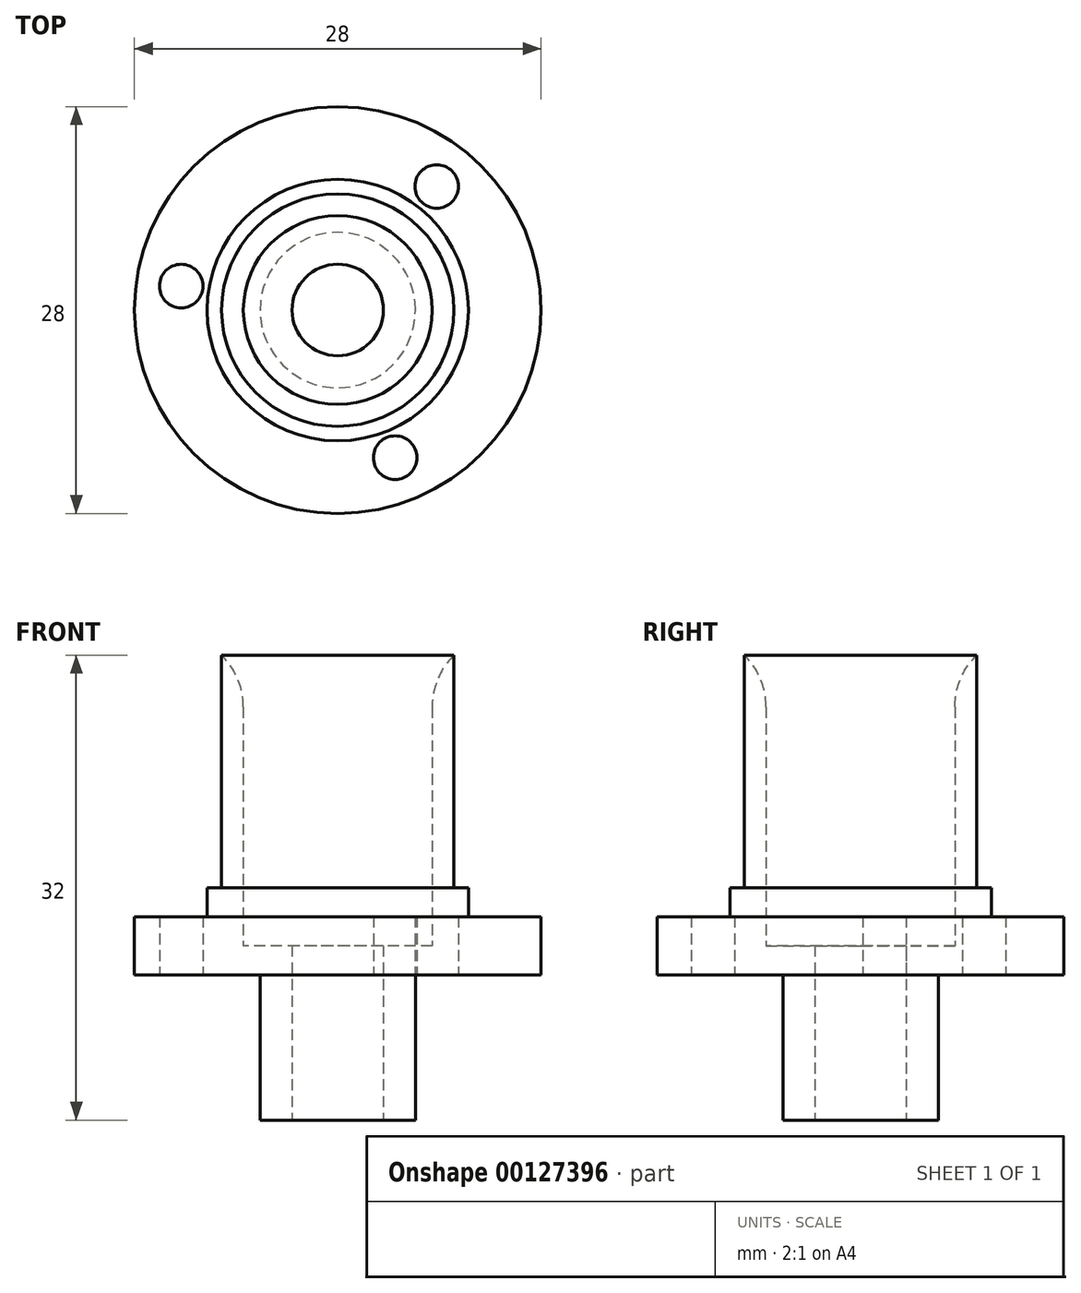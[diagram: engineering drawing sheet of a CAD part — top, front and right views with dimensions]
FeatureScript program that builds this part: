
annotation { "Feature Type Name" : "Feature", "Feature Type Description" : "" }
export const myFeature = defineFeature(function(context is Context, id is Id, definition is map)
    precondition{}
    {
        {
            var Q0;
            Q0=qCreatedBy(makeId("Top.planeOp"),FACE);
            var sketch = newSketch(context, id + "F0", { "sketchPlane" : qUnion([Q0])});
            skCircle(sketch, "E0", {"center": v(0, 0) * mm, "radius": 14 * mm});
            skCircle(sketch, "E1", {"center": v(0, 0) * mm, "radius": 3.15 * mm});
            skSolve(sketch);
        }
        {
            var Q0;
            Q0=makeQuery(id+"F0.imprint","IMPRINT",FACE,{"disambiguationData":[TD([[makeQuery(id+"F0.imprint","IMPRINT",EDGE,{"derivedFrom":sQuery(id+"F0.wireOp",EDGE,"E0")}),1.0]])]});
            extrude(context, id + "F1", {"entities" : qUnion([Q0]), "depth" : 4 * mm});
        }
        {
            var Q0;
            Q0=qCreatedBy(makeId("Top.planeOp"),FACE);
            var sketch = newSketch(context, id + "F2", { "sketchPlane" : qUnion([Q0])});
            skCircle(sketch, "E2", {"center": v(0, 0) * mm, "radius": 9 * mm});
            skSolve(sketch);
        }
        {
            var Q0;
            Q0=makeQuery(id+"F2.imprint","IMPRINT",FACE,{"disambiguationData":[TD([[makeQuery(id+"F2.imprint","IMPRINT",EDGE,{"derivedFrom":sQuery(id+"F2.wireOp",EDGE,"E2")}),1.0]])]});
            extrude(context, id + "F3", {"entities" : qUnion([Q0]), "operationType" : NewBodyOperationType.ADD, "depth" : 6 * mm});
        }
        {
            var Q0;
            Q0=qCreatedBy(makeId("Top.planeOp"),FACE);
            var sketch = newSketch(context, id + "F4", { "sketchPlane" : qUnion([Q0])});
            skCircle(sketch, "E3", {"center": v(0, 0) * mm, "radius": 8 * mm});
            skSolve(sketch);
        }
        {
            var Q0;
            Q0=makeQuery(id+"F4.imprint","IMPRINT",FACE,{"disambiguationData":[TD([[makeQuery(id+"F4.imprint","IMPRINT",EDGE,{"derivedFrom":sQuery(id+"F4.wireOp",EDGE,"E3")}),1.0]])]});
            extrude(context, id + "F5", {"entities" : qUnion([Q0]), "operationType" : NewBodyOperationType.ADD, "depth" : 22 * mm});
        }
        {
            var Q0;
            Q0=qCreatedBy(makeId("Top.planeOp"),FACE);
            var sketch = newSketch(context, id + "F6", { "sketchPlane" : qUnion([Q0])});
            skCircle(sketch, "E4", {"center": v(0, 0) * mm, "radius": 6.5 * mm});
            skSolve(sketch);
        }
        {
            var Q0;
            Q0=makeQuery(id+"F6.imprint","IMPRINT",FACE,{"disambiguationData":[TD([[makeQuery(id+"F6.imprint","IMPRINT",EDGE,{"derivedFrom":sQuery(id+"F6.wireOp",EDGE,"E4")}),1.0]])]});
            extrude(context, id + "F7", {"entities" : qUnion([Q0]), "operationType" : NewBodyOperationType.REMOVE, "depth" : 25 * mm});
        }
        {
            var Q0;
            Q0=qCreatedBy(makeId("Top.planeOp"),FACE);
            var sketch = newSketch(context, id + "F8", { "sketchPlane" : qUnion([Q0])});
            skCircle(sketch, "E5.cCircle", {"center": v(0, 0) * mm, "radius": 10.9 * mm, "construction": true});
            skLineSegment(sketch, "E5.0", {"start": v(-10.77, 1.65) * mm, "end": v(6.82, 8.5) * mm});
            skLineSegment(sketch, "E5.1", {"start": v(6.82, 8.5) * mm, "end": v(3.96, -10.16) * mm});
            skLineSegment(sketch, "E5.2", {"start": v(3.96, -10.16) * mm, "end": v(-10.77, 1.65) * mm});
            skCircle(sketch, "E6", {"center": v(3.96, -10.16) * mm, "radius": 1.5 * mm});
            skCircle(sketch, "E7", {"center": v(6.82, 8.5) * mm, "radius": 1.5 * mm});
            skCircle(sketch, "E8", {"center": v(-10.77, 1.65) * mm, "radius": 1.5 * mm});
            skSolve(sketch);
        }
        {
            var Q0;
            Q0=qCreatedBy(makeId("Top.planeOp"),FACE);
            var sketch = newSketch(context, id + "F9", { "sketchPlane" : qUnion([Q0])});
            skCircle(sketch, "E9", {"center": v(0, 0) * mm, "radius": 3.15 * mm});
            skCircle(sketch, "E10", {"center": v(0, 0) * mm, "radius": 5.35 * mm});
            skSolve(sketch);
        }
        {
            var Q0;
            Q0=makeQuery(id+"F0.imprint","IMPRINT",FACE,{"disambiguationData":[TD([[makeQuery(id+"F0.imprint","IMPRINT",EDGE,{"derivedFrom":sQuery(id+"F0.wireOp",EDGE,"E0")}),1.0]])]});
            extrude(context, id + "F10", {"entities" : qUnion([Q0]), "operationType" : NewBodyOperationType.ADD, "depth" : 2 * mm});
        }
        {
            var Q0;
            {var subQ0=sQuery(id+"F8.wireOp",EDGE,"E5.2");var subQ1=sQuery(id+"F8.wireOp",EDGE,"E5.1");var subQ2=makeQuery(id+"F8.imprint","INTERSECT",VERTEX,{"derivedFrom":[subQ1,subQ0]});Q0=makeQuery(id+"F8.imprint","IMPRINT",FACE,{"disambiguationData":[TD([[makeQuery(id+"F8.imprint","IMPRINT",EDGE,{"disambiguationData":[TD([[subQ2,1.0]])],"derivedFrom":subQ1}),1.0]])]});}
            var Q1;
            {var subQ0=sQuery(id+"F8.wireOp",EDGE,"E5.2");var subQ1=sQuery(id+"F8.wireOp",EDGE,"E5.1");var subQ2=makeQuery(id+"F8.imprint","INTERSECT",VERTEX,{"derivedFrom":[subQ1,subQ0]});Q1=makeQuery(id+"F8.imprint","IMPRINT",FACE,{"disambiguationData":[TD([[makeQuery(id+"F8.imprint","IMPRINT",EDGE,{"disambiguationData":[TD([[subQ2,1.0]])],"derivedFrom":subQ1}),-1.0]])]});}
            var Q2;
            {var subQ0=sQuery(id+"F8.wireOp",EDGE,"E5.2");var subQ1=sQuery(id+"F8.wireOp",EDGE,"E5.0");var subQ2=makeQuery(id+"F8.imprint","INTERSECT",VERTEX,{"derivedFrom":[subQ1,subQ0]});Q2=makeQuery(id+"F8.imprint","IMPRINT",FACE,{"disambiguationData":[TD([[makeQuery(id+"F8.imprint","IMPRINT",EDGE,{"disambiguationData":[TD([[subQ2,-1.0]])],"derivedFrom":subQ1}),1.0]])]});}
            var Q3;
            {var subQ0=sQuery(id+"F8.wireOp",EDGE,"E5.2");var subQ1=sQuery(id+"F8.wireOp",EDGE,"E5.0");var subQ2=makeQuery(id+"F8.imprint","INTERSECT",VERTEX,{"derivedFrom":[subQ1,subQ0]});Q3=makeQuery(id+"F8.imprint","IMPRINT",FACE,{"disambiguationData":[TD([[makeQuery(id+"F8.imprint","IMPRINT",EDGE,{"disambiguationData":[TD([[subQ2,-1.0]])],"derivedFrom":subQ1}),-1.0]])]});}
            var Q4;
            {var subQ0=sQuery(id+"F8.wireOp",EDGE,"E5.1");var subQ1=sQuery(id+"F8.wireOp",EDGE,"E5.0");var subQ2=makeQuery(id+"F8.imprint","INTERSECT",VERTEX,{"derivedFrom":[subQ1,subQ0]});Q4=makeQuery(id+"F8.imprint","IMPRINT",FACE,{"disambiguationData":[TD([[makeQuery(id+"F8.imprint","IMPRINT",EDGE,{"disambiguationData":[TD([[subQ2,1.0]])],"derivedFrom":subQ1}),1.0]])]});}
            var Q5;
            {var subQ0=sQuery(id+"F8.wireOp",EDGE,"E5.1");var subQ1=sQuery(id+"F8.wireOp",EDGE,"E5.0");var subQ2=makeQuery(id+"F8.imprint","INTERSECT",VERTEX,{"derivedFrom":[subQ1,subQ0]});Q5=makeQuery(id+"F8.imprint","IMPRINT",FACE,{"disambiguationData":[TD([[makeQuery(id+"F8.imprint","IMPRINT",EDGE,{"disambiguationData":[TD([[subQ2,1.0]])],"derivedFrom":subQ1}),-1.0]])]});}
            extrude(context, id + "F11", {"entities" : qUnion([Q0, Q1, Q2, Q3, Q4, Q5]), "operationType" : NewBodyOperationType.REMOVE, "depth" : 25 * mm});
        }
        {
            var Q0;
            Q0=makeQuery(id+"F9.imprint","IMPRINT",FACE,{"disambiguationData":[TD([[makeQuery(id+"F9.imprint","IMPRINT",EDGE,{"derivedFrom":sQuery(id+"F9.wireOp",EDGE,"E9")}),-1.0]])]});
            extrude(context, id + "F12", {"entities" : qUnion([Q0]), "operationType" : NewBodyOperationType.ADD, "oppositeDirection" : true, "depth" : 10 * mm});
        }
        {
            var Q0;
            Q0=makeQuery(id+"F7.boolean.opBoolean","INTERSECT",EDGE,{"derivedFrom":[makeQuery(id+"F5.opExtrude","CAP_FACE",FACE,{"disambiguationData":[OSD([sQuery(id+"F4.wireOp",EDGE,"E3")])],"isStart":false}),makeQuery(id+"F7.opExtrude","SWEPT_FACE",FACE,{"disambiguationData":[OSD([sQuery(id+"F6.wireOp",EDGE,"E4")])]})]});
            fillet(context, id + "F13", {"entities" : qUnion([Q0]), "radius" : 5 * mm, "tangentPropagation" : true, "allowEdgeOverflow" : false});
        }
    });
